# Revit family: IS_Connect_E5045_BIM_DE
name_source: partatom
category: Plumbing Fixtures
revit_build: Autodesk Revit MEP 2016 (Build: 20161004_0715(x64)
units: mm (PartAtom-declared; Revit-internal decimal feet)

## family parameters
Always vertical = No
Cut with Voids When Loaded = No
OmniClass Number = 23.45.05.14.14
OmniClass Title = Sinks/Lavatories
Part Type = Normal
Room Calculation Point = No
Round Connector Dimension = Use Diameter
Shared = No
Work Plane-Based = No

## types (2) — shared parameters
Accessories = www.idealstandard.de\ersatzteile
AssetType = Fixed
BIMobject category = Basins
BOSUseNativeGeometries = 1
Brand = Ideal Standard
Brand url = http://www.idealstandard.de
CodePerformance = DIN EN 14688 CL 15, DIN EN 31
ConnectionType = Plumbing
CurrencyUnit = €
CurrentRevision = 1
DurationUnit = Jaar
EAN code = https://5017830446859
Edition number = 1
ExpectedLife = 25
Features = CONNECT countertop washbasin 480x350mm, no taphole, with overflow
IFC Classification = Sanitary Terminal
IfcExportAs = Sanitary terminal type
IfcExportType = WASHBASIN
Installation instructions = http://www.idealstandard.it
InstallationInstructions = www.idealstandard.de\produkte
LinearUnits = millimetres
MaintenanceInformation = www.idealstandard.de
Manufacturer = http://www.idealstandard.de
Manufacturer name = Ideal Standard
ManufacturerURL = http://www.idealstandard.de
Material = Vitreous china
Material main = Ceramics
NBS Reference Code = 35-79-18
NBS Reference Description = Counter Top Wash Basins
NettWeight = 5,943 kg
Nominal height = 175
Nominal width = 480
NominalHeight = 175 mm  [stored 0.574147 ft]
NominalLength = 350 mm
NominalWidth = 480 mm  [stored 1.5748 ft]
OmniClass Code = 23-31 13 00
OmniClass Description = Sinks
Product Guid = 2344e846-e566-4679-9031-3155df70c984
Product SKU = E5045
Product certification = DIN EN 14688 CL 15, DIN EN 31
Product data url = https://bimobject.com
Product family = CONNECT
Product group = Basin
Product name = CONNECT COUNTERTOP BASIN 48X35 WHITEIP NTH OVAL
Product url = http://www.idealstandard.it
ProductInformation = www.idealstandard.de/produkte
QR code = http://bimobject.com
Shape = Sculptured
Size = 480x350x175 mm
Space = Internal
SpareParts = www.idealstandard.de/ersatzteile
Technical description = http://www.idealstandard.it
URL = http://www.idealstandard.de
Uniclass 1.4 Code = L7212
Uniclass 1.4 Description = Washbasins
Uniclass 2.0 Code = PR-35-79-94
Uniclass 2.0 Description = Wall-Hung Wash Basins
Uniclass 2015 Code = Pr_40_20_96_96
Uniclass 2015 Name = Wall-hung wash basins
Uniclass2015Code = Pr_40_20_96_18
Uniclass2015Title = Counter top wash basins
Uniclass2015Version = Products v1.1
VolumeUnits = Litres
WashHandBasinMounting = Countertop
WashHandBasinType = Hand Rinse
Weight Net (Kg) = 5.94
zero-valued in all types: Cost, DrainSize

## per-type parameters (varying)
| type | BIMObjectName | BarCode | Color | Finish | MainColor | Model | ModelNumber | Name |
| E504501 CONNECT countertop washbasin 480x350mm, no taphole, with overflow | ISI_IdealStandard_CounterTopWashbasins_CONNECT_E504501 | 5017830446859 | White | White | White | E504501 | E504501 | ISI_IdealStandard_CounterTopWashbasins_CONNECT_E504501 |
| E5045MA CONNECT countertop washbasin 480x350mm, no taphole, with overflow | ISI_IdealStandard_CounterTopWashbasins_CONNECT_E5045MA | 5017830446866 | WHITE IP | WHITE IP | WHITE IP | E5045MA | E5045MA | ISI_IdealStandard_CounterTopWashbasins_CONNECT_E5045MA |

note: column(s) folded — value = type name in every type: Description, ModelReference

note: [stored X ft] marks values corroborated as IEEE doubles in the binary element streams (Revit-internal decimal feet)

## geometry (parser evidence)
native form markers: Blend x4
no freeform markers — native parametric forms only
